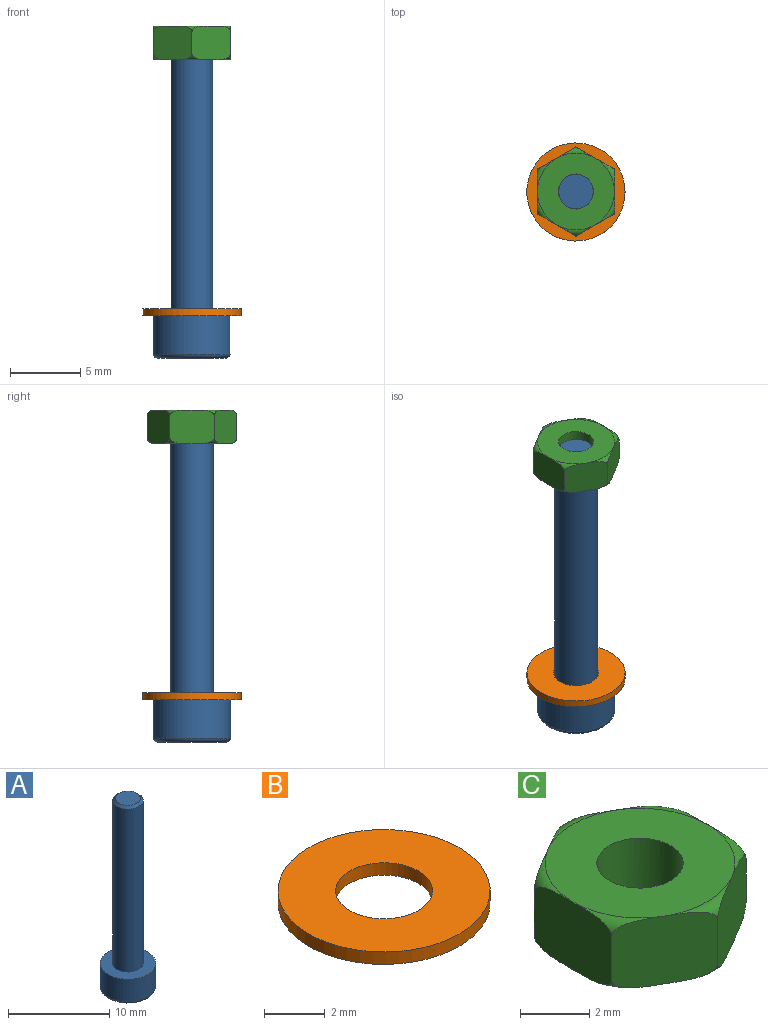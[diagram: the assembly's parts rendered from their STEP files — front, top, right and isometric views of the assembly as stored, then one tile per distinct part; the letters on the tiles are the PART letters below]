
ASSEMBLY  parts=3 mates=3
PART A: 14 faces, bbox 6x6x23 mm
  f0: plane 4.95x4.95mm, normal (0,0,-1), area 13.5mm2, adj f3,f4,f5,f6,f7,f8,f9
  f1: cylinder r=2.75mm len=5.5mm, axis (0,0,1), area 47.1mm2, adj f2,f3
  f2: plane 5.5x5.5mm, normal (0,0,1), area 16.7mm2, adj f1,f11
  f3: torus R=2.48mm, axis (0,0,-1), area 7.2mm2, adj f0,f1
  f4: plane 1.5x1.49mm, normal (-1,0,0), area 2.2mm2, adj f0,f5,f9,f10
  f5: plane 1.5x1.29mm, normal (-0.5,-0.87,0), area 2.2mm2, adj f0,f4,f6,f10
  f6: plane 1.5x1.29mm, normal (0.5,-0.87,0), area 2.2mm2, adj f0,f5,f7,f10
  f7: plane 1.5x1.49mm, normal (1,0,0), area 2.2mm2, adj f0,f6,f8,f10
  f8: plane 1.5x1.29mm, normal (0.5,0.87,0), area 2.2mm2, adj f0,f7,f9,f10
  f9: plane 1.5x1.29mm, normal (-0.5,0.87,0), area 2.2mm2, adj f0,f4,f8,f10
  f10: plane 2.98x2.58mm, normal (0,0,-1), area 5.8mm2, adj f4,f5,f6,f7,f8,f9
  f11: cylinder r=1.5mm len=19.73mm, axis (0,0,-1), area 185.9mm2, adj f2,f13
  f12: plane 2.46x2.46mm, normal (0,0,1), area 4.7mm2, adj f13
  f13: cone r=1.23mm half-angle=45deg, axis (0,0,-1), area 3.3mm2, adj f11,f12
PART B: 4 faces, bbox 7x7x0.5 mm
  f0: cylinder r=1.6mm len=3.2mm, axis (0,0,-1), area 5mm2, adj f2,f3
  f1: cylinder r=3.5mm len=7mm, axis (0,0,-1), area 11mm2, adj f2,f3
  f2: plane 7x7mm, normal (0,0,1), area 30.4mm2, adj f0,f1
  f3: plane 7x7mm, normal (0,0,-1), area 30.4mm2, adj f0,f1
PART C: 11 faces, bbox 6.9x6.9x2.4 mm
  f0: plane 5.49x5.49mm, normal (0,0,1), area 18.8mm2, adj f1,f10
  f1: torus R=2.75mm, axis (0,0,-1), area 2.8mm2, adj f0,f2,f3,f4,f5,f6,f7
  f2: plane 2.75x2.4mm, normal (0.5,0.87,0), area 7.3mm2, adj f1,f3,f7,f9
  f3: plane 3.18x2.4mm, normal (1,0,0), area 7.3mm2, adj f1,f2,f4,f9
  f4: plane 2.75x2.4mm, normal (0.5,-0.87,0), area 7.3mm2, adj f1,f3,f5,f9
  f5: plane 2.75x2.4mm, normal (-0.5,-0.87,0), area 7.3mm2, adj f1,f4,f6,f9
  f6: plane 3.18x2.4mm, normal (-1,0,0), area 7.3mm2, adj f1,f5,f7,f9
  f7: plane 2.75x2.4mm, normal (-0.5,0.87,0), area 7.3mm2, adj f1,f2,f6,f9
  f8: plane 5.49x5.49mm, normal (0,0,-1), area 18.8mm2, adj f9,f10
  f9: torus R=2.75mm, axis (0,0,-1), area 2.8mm2, adj f2,f3,f4,f5,f6,f7,f8
  f10: cylinder r=1.25mm len=2.5mm, axis (0,0,-1), area 18.8mm2, adj f0,f8
PLACE A t=(0,0,-9.61)mm
PLACE B t=(70,10,-9.61)mm
PLACE C t=(40,20,8.66)mm
MATE cylindrical A.f1 <-> B.f0  axis (0,0,-1) through (60,0,0.25)mm
MATE planar B.f0 <-> A.f1  axis (0,0,-1) through (60,0,-9.61)mm
MATE cylindrical C.f1 <-> A.f1  axis (0,0,-1) through (60,0,9.86)mm
